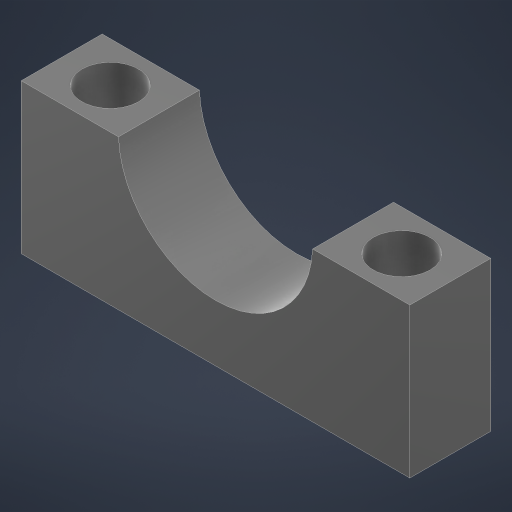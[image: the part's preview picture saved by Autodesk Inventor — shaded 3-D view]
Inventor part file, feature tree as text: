
AUTODESK INVENTOR PART (.ipt)
format: ipt  version: 2024.1 (Build 281209000, 209)  size: 184,832 bytes
history: native  units: mm
features: extrude x2
ambient origin geometry x8: Origin, YZ Plane, XZ Plane, XY Plane, X Axis, Y Axis, Z Axis, Center Point
bodies: Solid1 (feature_tree)
feature tree (2):
  extrude  "Extrusion1"  Depth=12.0mm
  extrude  "Extrusion2"  Depth=24.0mm
